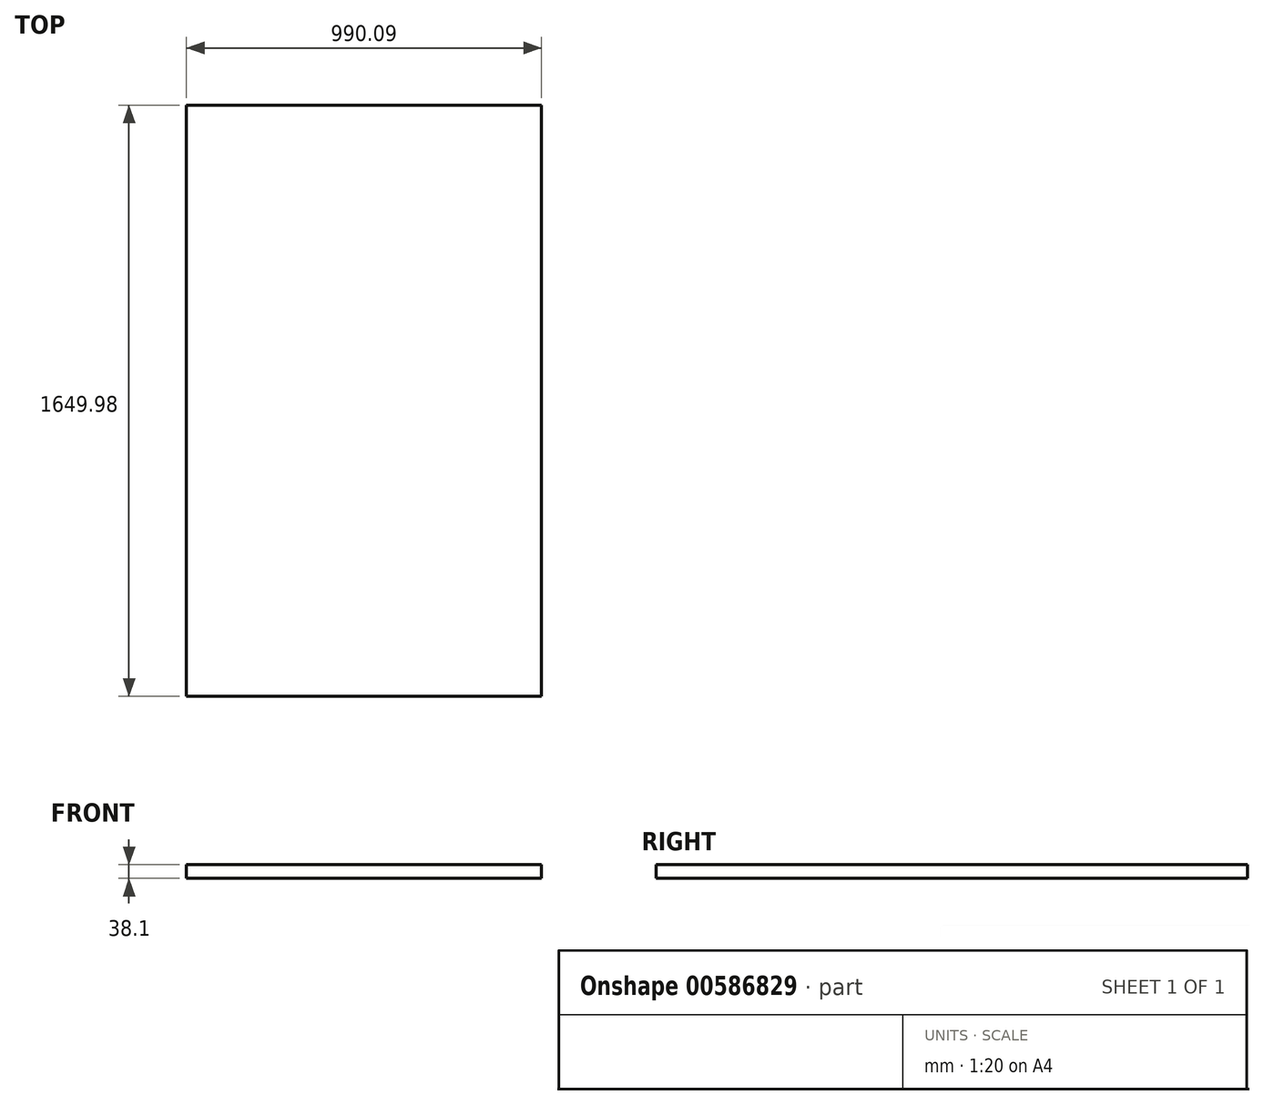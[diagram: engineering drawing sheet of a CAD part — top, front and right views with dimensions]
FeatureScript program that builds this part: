
annotation { "Feature Type Name" : "Feature", "Feature Type Description" : "" }
export const myFeature = defineFeature(function(context is Context, id is Id, definition is map)
    precondition{}
    {
        {
            var Q0;
            Q0=qCreatedBy(makeId("Top.planeOp"),FACE);
            var sketch = newSketch(context, id + "F0", { "sketchPlane" : qUnion([Q0])});
            skLineSegment(sketch, "E0.bottom", {"start": v(-801.93, 819.26) * mm, "end": v(188.16, 819.26) * mm});
            skLineSegment(sketch, "E0.top", {"start": v(-801.93, -830.72) * mm, "end": v(188.16, -830.72) * mm});
            skLineSegment(sketch, "E0.left", {"start": v(-801.93, 819.26) * mm, "end": v(-801.93, -830.72) * mm});
            skLineSegment(sketch, "E0.right", {"start": v(188.16, 819.26) * mm, "end": v(188.16, -830.72) * mm});
            skSolve(sketch);
        }
        {
            var Q0;
            Q0 = qSketchRegion(id + "F0", true);
            extrude(context, id + "F1", {"entities" : qUnion([Q0]), "depth" : 38.1 * mm, "offsetDistance" : 25.4 * mm});
        }
    });
